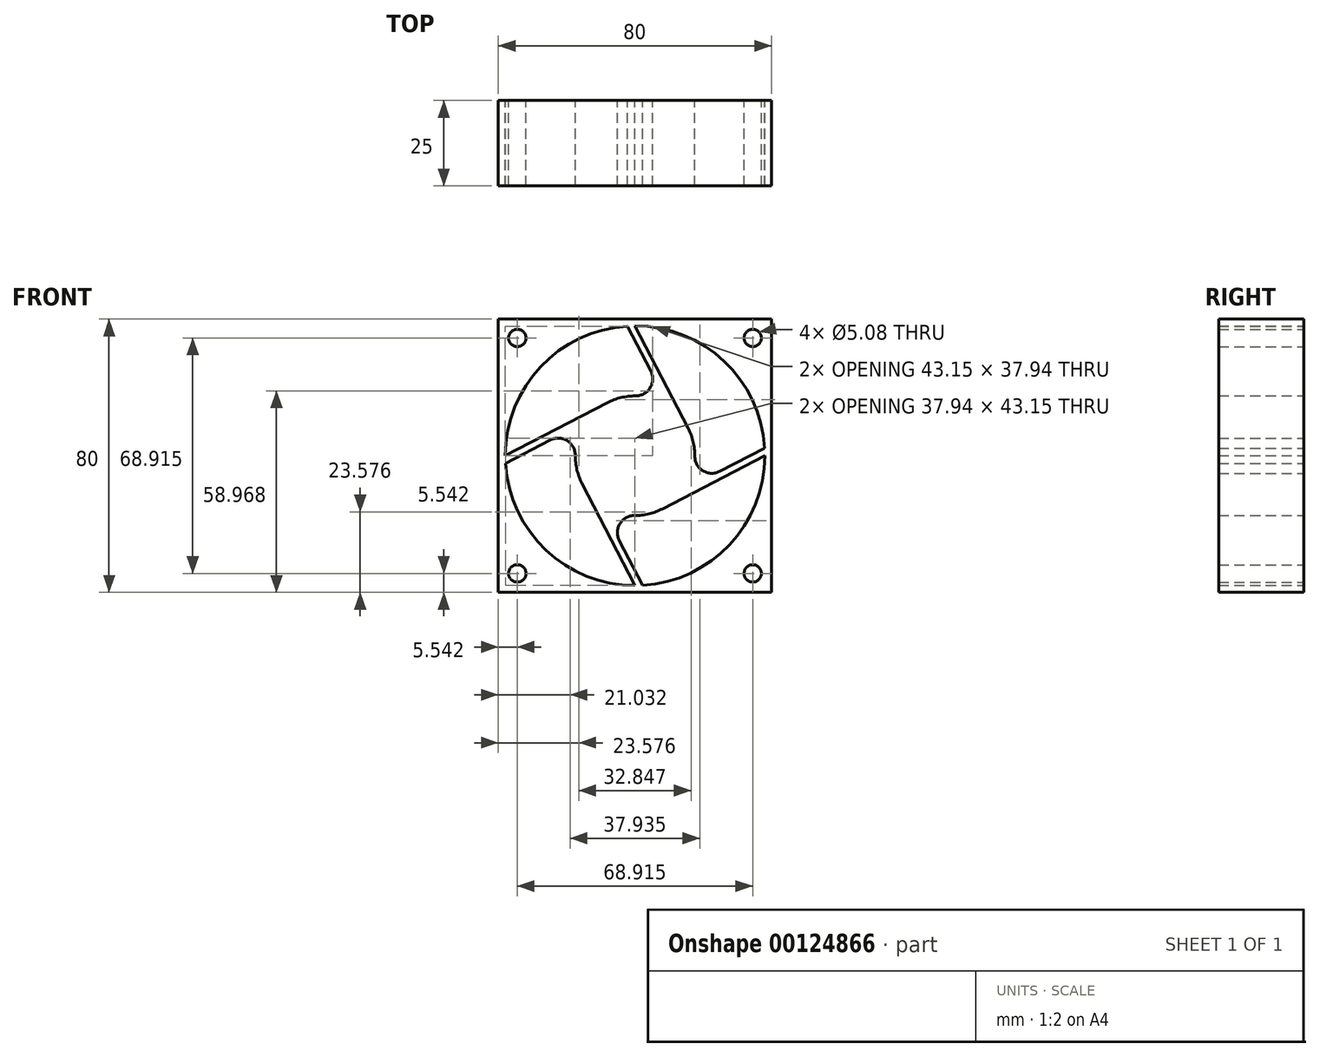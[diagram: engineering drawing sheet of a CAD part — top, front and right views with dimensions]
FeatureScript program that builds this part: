
annotation { "Feature Type Name" : "Feature", "Feature Type Description" : "" }
export const myFeature = defineFeature(function(context is Context, id is Id, definition is map)
    precondition{}
    {
        {
            var Q0;
            Q0=qCreatedBy(makeId("Front.planeOp"),FACE);
            var sketch = newSketch(context, id + "F0", { "sketchPlane" : qUnion([Q0])});
            skArc(sketch, "E0", {"start": v(-14.35, 10.02) * mm, "mid": v(-17.46, 1.14) * mm, "end": v(-15.53, -8.06) * mm});
            skArc(sketch, "E1", {"start": v(-37.94, -2.22) * mm, "mid": v(-26.07, -27.64) * mm, "end": v(0, -38) * mm});
            skLineSegment(sketch, "E2.bottom", {"start": v(40, -40) * mm, "end": v(-40, -40) * mm});
            skLineSegment(sketch, "E2.top", {"start": v(40, 40) * mm, "end": v(-40, 40) * mm});
            skLineSegment(sketch, "E2.left", {"start": v(40, -40) * mm, "end": v(40, 40) * mm});
            skLineSegment(sketch, "E2.right", {"start": v(-40, -40) * mm, "end": v(-40, 40) * mm});
            skLineSegment(sketch, "E3", {"start": v(-46.91, 0) * mm, "end": v(43.29, 0) * mm, "construction": true});
            skPoint(sketch, "E3.startSnap0", {"position": v(-40, 0) * mm});
            skPoint(sketch, "E3.endSnap0", {"position": v(40, 0) * mm});
            skLineSegment(sketch, "E4", {"start": v(0, 46.3) * mm, "end": v(0, -49.43) * mm, "construction": true});
            skPoint(sketch, "E5", {"position": v(0, 38) * mm});
            skPoint(sketch, "E6", {"position": v(-38, 0) * mm});
            skLineSegment(sketch, "E7", {"start": v(0, 38) * mm, "end": v(15.53, 8.06) * mm});
            skLineSegment(sketch, "E8", {"start": v(38, 0) * mm, "end": v(8.06, -15.53) * mm});
            skLineSegment(sketch, "E9", {"start": v(0, -38) * mm, "end": v(-15.53, -8.06) * mm});
            skLineSegment(sketch, "E10", {"start": v(-38, 0) * mm, "end": v(-8.06, 15.53) * mm});
            skLineSegment(sketch, "E11.0", {"start": v(-2.22, 37.94) * mm, "end": v(10.02, 14.35) * mm});
            skLineSegment(sketch, "E12.0", {"start": v(37.94, 2.22) * mm, "end": v(14.35, -10.02) * mm});
            skLineSegment(sketch, "E13.0", {"start": v(2.22, -37.94) * mm, "end": v(-10.02, -14.35) * mm});
            skLineSegment(sketch, "E14.0", {"start": v(-37.94, -2.22) * mm, "end": v(-14.35, 10.02) * mm});
            skPoint(sketch, "E15.orphan", {"position": v(0, -19.72) * mm});
            skArc(sketch, "E16.trimOffspring", {"start": v(10.02, 14.35) * mm, "mid": v(1.14, 17.46) * mm, "end": v(-8.06, 15.53) * mm});
            skArc(sketch, "E17.trimOffspring", {"start": v(-2.22, 37.94) * mm, "mid": v(-27.64, 26.07) * mm, "end": v(-38, 0) * mm});
            skArc(sketch, "E18.trimOffspring", {"start": v(37.94, 2.22) * mm, "mid": v(26.07, 27.64) * mm, "end": v(0, 38) * mm});
            skArc(sketch, "E19.trimOffspring", {"start": v(14.35, -10.02) * mm, "mid": v(17.46, -1.14) * mm, "end": v(15.53, 8.06) * mm});
            skArc(sketch, "E20.trimOffspring", {"start": v(-10.02, -14.35) * mm, "mid": v(-1.14, -17.46) * mm, "end": v(8.06, -15.53) * mm});
            skArc(sketch, "E21.trimOffspring", {"start": v(2.22, -37.94) * mm, "mid": v(27.64, -26.07) * mm, "end": v(38, 0) * mm});
            skCircle(sketch, "E22", {"center": v(-34.46, -34.46) * mm, "radius": 2.54 * mm});
            skLineSegment(sketch, "E23", {"start": v(-34.46, -34.46) * mm, "end": v(-37, -34.46) * mm, "construction": true});
            skLineSegment(sketch, "E24", {"start": v(-34.46, -34.46) * mm, "end": v(-34.46, -37) * mm, "construction": true});
            skCircle(sketch, "E25.MirrorC", {"center": v(-34.46, 34.46) * mm, "radius": 2.54 * mm});
            skLineSegment(sketch, "E26.MirrorCS", {"start": v(0, -46.3) * mm, "end": v(0, 49.43) * mm, "construction": true});
            skCircle(sketch, "E27.MirrorC", {"center": v(34.46, 34.46) * mm, "radius": 2.54 * mm});
            skCircle(sketch, "E28.MirrorC", {"center": v(34.46, -34.46) * mm, "radius": 2.54 * mm});
            skSolve(sketch);
        }
        {
            var Q0;
            Q0=makeQuery(id+"F0.imprint","IMPRINT",FACE,{"disambiguationData":[TD([[makeQuery(id+"F0.imprint","IMPRINT",EDGE,{"derivedFrom":sQuery(id+"F0.wireOp",EDGE,"E0")}),1.0]])]});
            extrude(context, id + "F1", {"entities" : qUnion([Q0]), "depth" : 25 * mm, "symmetric" : true});
        }
        {
            var Q0;
            Q0=makeQuery(id+"F1.opExtrude","SWEPT_EDGE",EDGE,{"disambiguationData":[OSD([sQuery(id+"F0.wireOp",EDGE,"E11.0"),sQuery(id+"F0.wireOp",EDGE,"E16.trimOffspring")])]});
            var Q1;
            Q1=makeQuery(id+"F1.opExtrude","SWEPT_EDGE",EDGE,{"disambiguationData":[OSD([sQuery(id+"F0.wireOp",EDGE,"E0"),sQuery(id+"F0.wireOp",EDGE,"E14.0")])]});
            var Q2;
            Q2=makeQuery(id+"F1.opExtrude","SWEPT_EDGE",EDGE,{"disambiguationData":[OSD([sQuery(id+"F0.wireOp",EDGE,"E13.0"),sQuery(id+"F0.wireOp",EDGE,"E20.trimOffspring")])]});
            var Q3;
            Q3=makeQuery(id+"F1.opExtrude","SWEPT_EDGE",EDGE,{"disambiguationData":[OSD([sQuery(id+"F0.wireOp",EDGE,"E12.0"),sQuery(id+"F0.wireOp",EDGE,"E19.trimOffspring")])]});
            fillet(context, id + "F2", {"entities" : qUnion([Q0, Q1, Q2, Q3]), "radius" : 5 * mm, "tangentPropagation" : true, "allowEdgeOverflow" : false});
        }
    });
